FCSTD DOCUMENT  (FreeCAD 0.19R0.19.2)
Label: headphoneStandWithHookStudsRemoved
License: All rights reserved
LicenseURL: http://en.wikipedia.org/wiki/All_rights_reserved
objects: Sketcher::SketchObject×1
note: 1 computed .brp shape members not serialized (recipe doc carries the construction recipe); baked Part::Feature solids carry a one-line shape summary decoded from their .brp

FEATURE [Sketcher::SketchObject] Sketch
  FullyConstrained = false
  sketch-geometry (77):
    g0: LineSegment StartX=0 StartY=0 StartZ=0 EndX=-1.51927 EndY=0 EndZ=0
    g1: LineSegment StartX=0 StartY=5.04081 StartZ=0 EndX=-1.51927 EndY=5.04081 EndZ=0
    g2: LineSegment StartX=0 StartY=34.0653 StartZ=0 EndX=0 EndY=5.04081 EndZ=0
    g3: LineSegment StartX=0 StartY=39.1061 StartZ=0 EndX=-1.51927 EndY=39.1061 EndZ=0
    g4: LineSegment StartX=0 StartY=34.0653 StartZ=0 EndX=-1.51927 EndY=34.0653 EndZ=0
    g5: LineSegment StartX=0 StartY=73.1267 StartZ=0 EndX=-1.51927 EndY=73.1267 EndZ=0
    g6: LineSegment StartX=0 StartY=68.0859 StartZ=0 EndX=-1.51927 EndY=68.0859 EndZ=0
    g7: LineSegment StartX=0 StartY=68.0859 StartZ=0 EndX=0 EndY=39.1061 EndZ=0
    g8: LineSegment StartX=55.9714 StartY=45.0131 StartZ=0 EndX=47.9365 EndY=45.0131 EndZ=0
    g9: LineSegment StartX=0 StartY=73.1267 StartZ=0 EndX=0 EndY=78.2549 EndZ=0
    g10: LineSegment StartX=0 StartY=78.2549 StartZ=0 EndX=1.02877 EndY=78.2549 EndZ=0
    g11: Circle CenterX=1.02877 CenterY=78.2549 CenterZ=0 NormalX=0 NormalY=0 NormalZ=1 AngleXU=0 Radius=1
    g12: Circle CenterX=7.98777 CenterY=61.6212 CenterZ=0 NormalX=0 NormalY=0 NormalZ=1 AngleXU=0 Radius=1
    g13: Circle CenterX=7.98777 CenterY=45.0131 CenterZ=0 NormalX=0 NormalY=0 NormalZ=1 AngleXU=0 Radius=1
    g14: BSplineCurve PolesCount=3 KnotsCount=2 Degree=2 IsPeriodic=0
    g15: GeomPoint X=1.02877 Y=78.2549 Z=0
    g16: GeomPoint X=7.98777 Y=45.0131 Z=0
    g17: Circle CenterX=7.98777 CenterY=36.0353 CenterZ=0 NormalX=0 NormalY=0 NormalZ=1 AngleXU=0 Radius=1
    g18: Circle CenterX=7.98777 CenterY=32.5409 CenterZ=0 NormalX=0 NormalY=0 NormalZ=1 AngleXU=0 Radius=1
    g19: Circle CenterX=11.4386 CenterY=31.9944 CenterZ=0 NormalX=0 NormalY=0 NormalZ=1 AngleXU=0 Radius=1
    g20: BSplineCurve PolesCount=3 KnotsCount=2 Degree=2 IsPeriodic=0
    g21: GeomPoint X=7.98777 Y=36.0353 Z=0
    g22: GeomPoint X=11.4386 Y=31.9944 Z=0
    g23: LineSegment StartX=7.98777 StartY=45.0131 StartZ=0 EndX=7.98777 EndY=36.0353 EndZ=0
    g24: Circle CenterX=47.9365 CenterY=36.0282 CenterZ=0 NormalX=0 NormalY=0 NormalZ=1 AngleXU=0 Radius=1
    g25: Circle CenterX=47.9365 CenterY=32.4999 CenterZ=0 NormalX=0 NormalY=0 NormalZ=1 AngleXU=0 Radius=1
    g26: Circle CenterX=44.5192 CenterY=31.9623 CenterZ=0 NormalX=0 NormalY=0 NormalZ=1 AngleXU=0 Radius=1
    g27: BSplineCurve PolesCount=3 KnotsCount=2 Degree=2 IsPeriodic=0
    g28: GeomPoint X=47.9365 Y=36.0282 Z=0
    g29: GeomPoint X=44.5192 Y=31.9623 Z=0
    g30: LineSegment StartX=47.9365 StartY=45.0131 StartZ=0 EndX=47.9365 EndY=36.0282 EndZ=0
    g31: Circle CenterX=11.4386 CenterY=31.9944 CenterZ=0 NormalX=0 NormalY=0 NormalZ=1 AngleXU=0 Radius=1
    g32: Circle CenterX=28.035 CenterY=29.0677 CenterZ=0 NormalX=0 NormalY=0 NormalZ=1 AngleXU=0 Radius=1
    g33: Circle CenterX=44.5192 CenterY=31.9623 CenterZ=0 NormalX=0 NormalY=0 NormalZ=1 AngleXU=0 Radius=1
    g34: BSplineCurve PolesCount=3 KnotsCount=2 Degree=2 IsPeriodic=0
    g35: GeomPoint X=11.4386 Y=31.9944 Z=0
    g36: GeomPoint X=44.5192 Y=31.9623 Z=0
    g37: Circle CenterX=52.4303 CenterY=20.0333 CenterZ=0 NormalX=0 NormalY=0 NormalZ=1 AngleXU=0 Radius=1
    g38: Circle CenterX=55.9714 CenterY=20.0333 CenterZ=0 NormalX=0 NormalY=0 NormalZ=1 AngleXU=0 Radius=1
    g39: Circle CenterX=55.9714 CenterY=23.539 CenterZ=0 NormalX=0 NormalY=0 NormalZ=1 AngleXU=0 Radius=1
    g40: BSplineCurve PolesCount=3 KnotsCount=2 Degree=2 IsPeriodic=0
    g41: GeomPoint X=52.4303 Y=20.0333 Z=0
    g42: GeomPoint X=55.9714 Y=23.539 Z=0
    g43: LineSegment StartX=0 StartY=-20.2076 StartZ=0 EndX=0.983266 EndY=-20.2076 EndZ=0
    g44: LineSegment StartX=0 StartY=0 StartZ=0 EndX=0 EndY=-20.2076 EndZ=0
    g45: Circle CenterX=4.47075 CenterY=-13.2519 CenterZ=0 NormalX=0 NormalY=0 NormalZ=1 AngleXU=0 Radius=1
    g46: Circle CenterX=9.98794 CenterY=10.1697 CenterZ=0 NormalX=0 NormalY=0 NormalZ=1 AngleXU=0 Radius=1
    g47: Circle CenterX=52.4303 CenterY=20.0333 CenterZ=0 NormalX=0 NormalY=0 NormalZ=1 AngleXU=0 Radius=1
    g48: BSplineCurve PolesCount=3 KnotsCount=2 Degree=2 IsPeriodic=0
    g49: GeomPoint X=4.47075 Y=-13.2519 Z=0
    g50: GeomPoint X=52.4303 Y=20.0333 Z=0
    g51-g55: Circle x5 (B-spline internal-alignment scaffolding for g56; pole/knot coordinates omitted)
    g56: BSplineCurve PolesCount=5 KnotsCount=3 Degree=3 IsPeriodic=0
    g57: GeomPoint X=0.983266 Y=-20.2076 Z=0
    g58: GeomPoint X=3.68451 Y=-17.8003 Z=0
    g59: GeomPoint X=4.47075 Y=-13.2519 Z=0
    g60: LineSegment StartX=55.9714 StartY=45.0131 StartZ=0 EndX=55.9714 EndY=23.539 EndZ=0
    g61: LineSegment StartX=-22.7998 StartY=4.1127 StartZ=0 EndX=-22.7998 EndY=9.24155 EndZ=0
    g62: LineSegment StartX=-22.8115 StartY=-0.928107 StartZ=0 EndX=-22.8115 EndY=-6.14103 EndZ=0
    g63: LineSegment StartX=-22.7998 StartY=9.24155 StartZ=0 EndX=-25.3277 EndY=9.24155 EndZ=0
    g64: LineSegment StartX=-22.8115 StartY=-6.14103 StartZ=0 EndX=-25.267 EndY=-6.14103 EndZ=0
    g65: Circle CenterX=-25.3277 CenterY=9.24139 CenterZ=0 NormalX=0 NormalY=0 NormalZ=1 AngleXU=0 Radius=1
    g66: Circle CenterX=-31.2766 CenterY=1.54417 CenterZ=0 NormalX=0 NormalY=0 NormalZ=1 AngleXU=0 Radius=1
    g67: Circle CenterX=-25.267 CenterY=-6.14103 CenterZ=0 NormalX=0 NormalY=0 NormalZ=1 AngleXU=0 Radius=1
    g68: BSplineCurve PolesCount=3 KnotsCount=2 Degree=2 IsPeriodic=0
    g69: GeomPoint X=-25.3277 Y=9.24139 Z=0
    g70: GeomPoint X=-25.267 Y=-6.14103 Z=0
    g71: LineSegment StartX=-21.2805 StartY=4.1127 StartZ=0 EndX=-22.7998 EndY=4.1127 EndZ=0
    g72: LineSegment StartX=-21.2805 StartY=-0.928107 StartZ=0 EndX=-22.8115 EndY=-0.928107 EndZ=0
    g73: LineSegment StartX=-21.2805 StartY=4.1127 StartZ=0 EndX=-21.2805 EndY=-0.928107 EndZ=0
    g74: LineSegment StartX=-1.51927 StartY=5.04081 StartZ=0 EndX=-1.51927 EndY=0 EndZ=0
    g75: LineSegment StartX=-1.51927 StartY=39.1061 StartZ=0 EndX=-1.51927 EndY=34.0653 EndZ=0
    g76: LineSegment StartX=-1.51927 StartY=73.1267 StartZ=0 EndX=-1.51927 EndY=68.0859 EndZ=0
  constraints (111):
    c: PointOnObject(g0,g-1)
    c: PointOnObject(g1,g-2)
    c: Horizontal(g1)
    c: Coincident(g2,g1)
    c: Vertical(g2)
    c: Horizontal(g3)
    c: Coincident(g4,g2)
    c: PointOnObject(g6,g-2)
    c: Horizontal(g5)
    c: Coincident(g7,g6)
    c: Horizontal(g8)
    c: Coincident(g9,g5)
    c: PointOnObject(g9,g-2)
    c: Vertical(g9)
    c: Coincident(g10,g9)
    c: Horizontal(g10)
    c: Coincident(g14,g10)
    c: Weight(g11) = 1
    c: Equal(g11,g12)
    c: Equal(g11,g13)
    c: InternalAlignment(g11,g14)
    c: InternalAlignment(g12,g14)
    c: InternalAlignment(g13,g14)
    c: InternalAlignment(g15,g14)
    c: InternalAlignment(g16,g14)
    c: Weight(g17) = 1
    c: Equal(g17,g18)
    c: Equal(g17,g19)
    c: InternalAlignment(g17,g20)
    c: InternalAlignment(g18,g20)
    c: InternalAlignment(g19,g20)
    c: InternalAlignment(g21,g20)
    c: InternalAlignment(g22,g20)
    c: Coincident(g23,g14)
    c: Coincident(g23,g20)
    c: Vertical(g23)
    c: Weight(g24) = 1
    c: Equal(g24,g25)
    c: Equal(g24,g26)
    c: InternalAlignment(g24,g27)
    c: InternalAlignment(g25,g27)
    c: InternalAlignment(g26,g27)
    c: InternalAlignment(g28,g27)
    c: InternalAlignment(g29,g27)
    c: Coincident(g30,g8)
    c: Coincident(g30,g27)
    c: Vertical(g30)
    c: Weight(g31) = 1
    c: Equal(g31,g32)
    c: Equal(g31,g33)
    c: InternalAlignment(g31,g34)
    c: InternalAlignment(g32,g34)
    c: InternalAlignment(g33,g34)
    c: InternalAlignment(g35,g34)
    c: InternalAlignment(g36,g34)
    c: Weight(g37) = 1
    c: Equal(g37,g38)
    c: Equal(g37,g39)
    c: InternalAlignment(g37,g40)
    c: InternalAlignment(g38,g40)
    c: InternalAlignment(g39,g40)
    c: InternalAlignment(g41,g40)
    c: InternalAlignment(g42,g40)
    c: Horizontal(g43)
    c: Coincident(g44,g0)
    c: Coincident(g44,g43)
    c: Vertical(g44)
    c: Weight(g45) = 1
    c: Equal(g45,g46)
    c: Equal(g45,g47)
    c: InternalAlignment(g45,g48)
    c: InternalAlignment(g46,g48)
    c: InternalAlignment(g47,g48)
    c: InternalAlignment(g49,g48)
    c: InternalAlignment(g50,g48)
    c: Coincident(g56,g43)
    c: Weight(g51) = 1
    c: Equal(g51, g52-g55) x4
    c: InternalAlignment(g51-g55 -> g56) x5
    c: InternalAlignment(g57,g56)
    c: InternalAlignment(g58,g56)
    c: InternalAlignment(g59,g56)
    c: Coincident(g60,g8)
    c: Coincident(g60,g40)
    c: Vertical(g60)
    c: Horizontal(g71)
    c: Coincident(g61,g71)
    c: Vertical(g61)
    c: Coincident(g62,g72)
    c: Vertical(g62)
    c: Coincident(g63,g61)
    c: Horizontal(g63)
    c: Coincident(g64,g62)
    c: Horizontal(g64)
    c: Weight(g65) = 1
    c: Equal(g65,g66)
    c: Equal(g65,g67)
    c: Coincident(g68,g64)
    c: InternalAlignment(g65,g68)
    c: InternalAlignment(g66,g68)
    c: InternalAlignment(g67,g68)
    c: Coincident(g73,g71)
    c: Coincident(g74,g1)
    c: Coincident(g74,g0)
    c: Vertical(g74)
    c: Coincident(g75,g3)
    c: Coincident(g75,g4)
    c: Vertical(g75)
    c: Coincident(g76,g5)
    c: Coincident(g76,g6)
    c: Vertical(g76)
